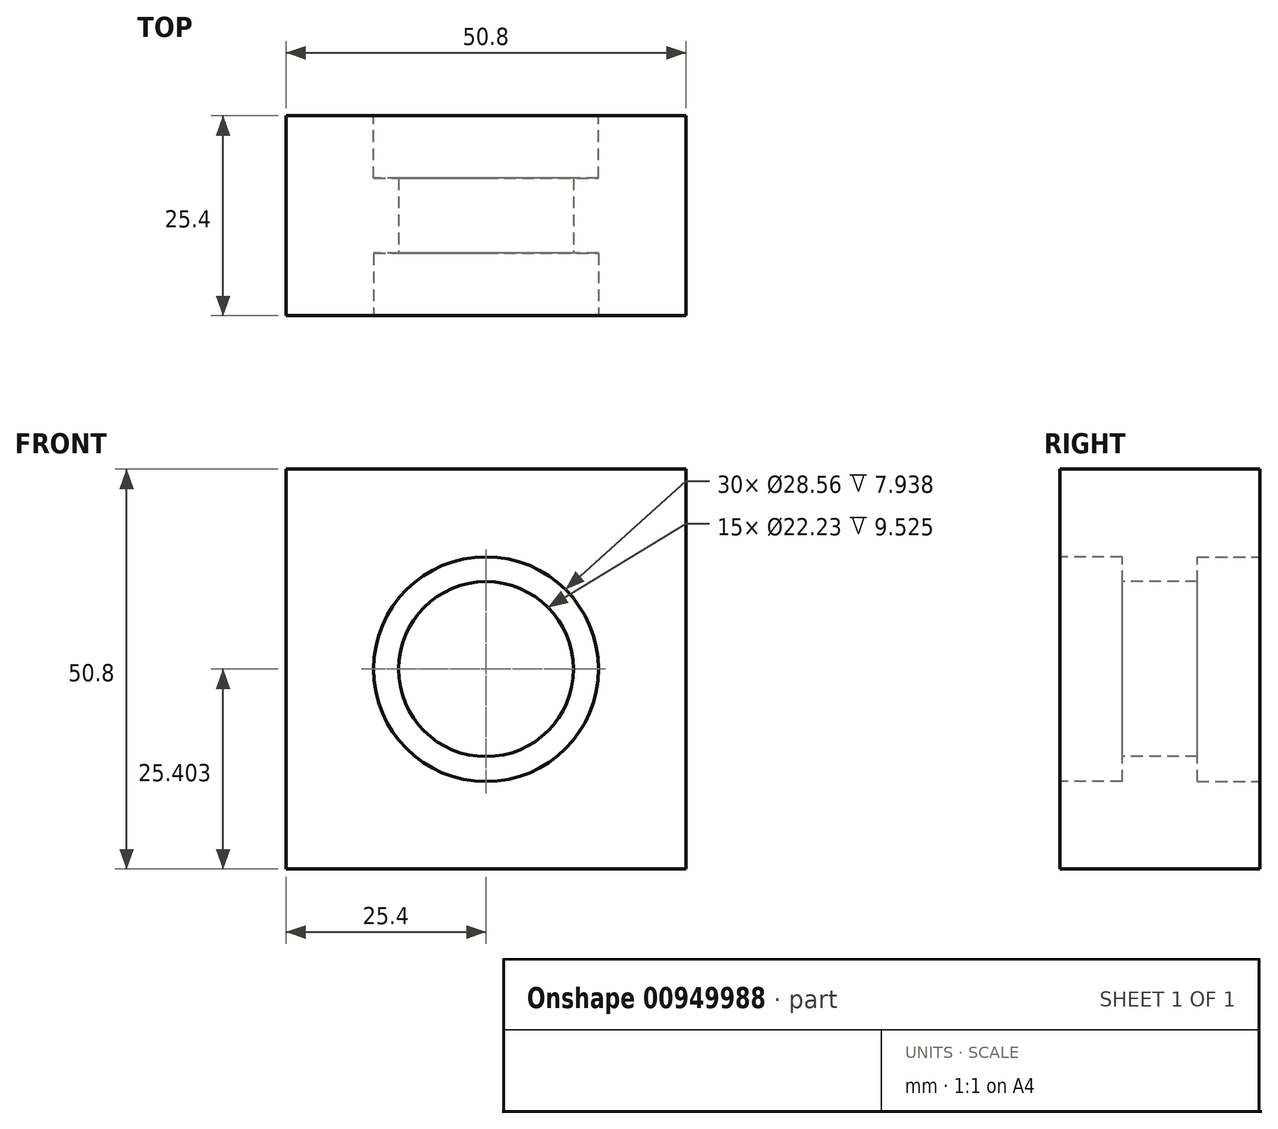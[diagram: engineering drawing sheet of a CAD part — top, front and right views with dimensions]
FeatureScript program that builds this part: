
annotation { "Feature Type Name" : "Feature", "Feature Type Description" : "" }
export const myFeature = defineFeature(function(context is Context, id is Id, definition is map)
    precondition{}
    {
        {
            var Q0;
            Q0=qCreatedBy(makeId("Front.planeOp"),FACE);
            var sketch = newSketch(context, id + "F0", { "sketchPlane" : qUnion([Q0])});
            skLineSegment(sketch, "E0.bottom", {"start": v(-50.8, 57.86) * mm, "end": v(0, 57.86) * mm});
            skLineSegment(sketch, "E0.top", {"start": v(-50.8, 7.06) * mm, "end": v(0, 7.06) * mm});
            skLineSegment(sketch, "E0.left", {"start": v(-50.8, 57.86) * mm, "end": v(-50.8, 7.06) * mm});
            skLineSegment(sketch, "E0.right", {"start": v(0, 57.86) * mm, "end": v(0, 7.06) * mm});
            skSolve(sketch);
        }
        {
            var Q0;
            Q0=qCreatedBy(makeId("Front.planeOp"),FACE);
            var sketch = newSketch(context, id + "F1", { "sketchPlane" : qUnion([Q0])});
            skCircle(sketch, "E1", {"center": v(-25.4, 32.46) * mm, "radius": 14.28 * mm});
            skSolve(sketch);
        }
        {
            var Q0;
            Q0 = qSketchRegion(id + "F0", true);
            extrude(context, id + "F2", {"entities" : qUnion([Q0]), "depth" : 25.4 * mm, "offsetDistance" : 25.4 * mm});
        }
        {
            var Q0;
            Q0 = qSketchRegion(id + "F1", true);
            extrude(context, id + "F3", {"entities" : qUnion([Q0]), "operationType" : NewBodyOperationType.REMOVE, "depth" : 7.94 * mm, "offsetDistance" : 25.4 * mm});
        }
        {
            var Q0;
            Q0=makeQuery(id+"F2.opExtrude","CAP_FACE",FACE,{"disambiguationData":[OSD([sQuery(id+"F0.wireOp",EDGE,"E0.bottom"),sQuery(id+"F0.wireOp",EDGE,"E0.top"),sQuery(id+"F0.wireOp",EDGE,"E0.left"),sQuery(id+"F0.wireOp",EDGE,"E0.right")])],"isStart":false});
            var sketch = newSketch(context, id + "F4", { "sketchPlane" : qUnion([Q0])});
            skCircle(sketch, "E2", {"center": v(-25.4, 32.46) * mm, "radius": 14.28 * mm});
            skSolve(sketch);
        }
        {
            var Q0;
            Q0 = qSketchRegion(id + "F4", true);
            extrude(context, id + "F5", {"entities" : qUnion([Q0]), "operationType" : NewBodyOperationType.REMOVE, "oppositeDirection" : true, "depth" : 7.94 * mm, "offsetDistance" : 25.4 * mm});
        }
        {
            var Q0;
            Q0=makeQuery(id+"F5.boolean.opBoolean","COPY",FACE,{"derivedFrom":makeQuery(id+"F5.opExtrude","CAP_FACE",FACE,{"disambiguationData":[OSD([sQuery(id+"F4.wireOp",EDGE,"E2")])],"isStart":false})});
            var sketch = newSketch(context, id + "F6", { "sketchPlane" : qUnion([Q0])});
            skCircle(sketch, "E3", {"center": v(-25.4, 32.46) * mm, "radius": 11.11 * mm});
            skSolve(sketch);
        }
        {
            var Q0;
            Q0 = qSketchRegion(id + "F6", true);
            extrude(context, id + "F7", {"entities" : qUnion([Q0]), "operationType" : NewBodyOperationType.REMOVE, "oppositeDirection" : true, "depth" : 25.4 * mm, "offsetDistance" : 25.4 * mm});
        }
    });
